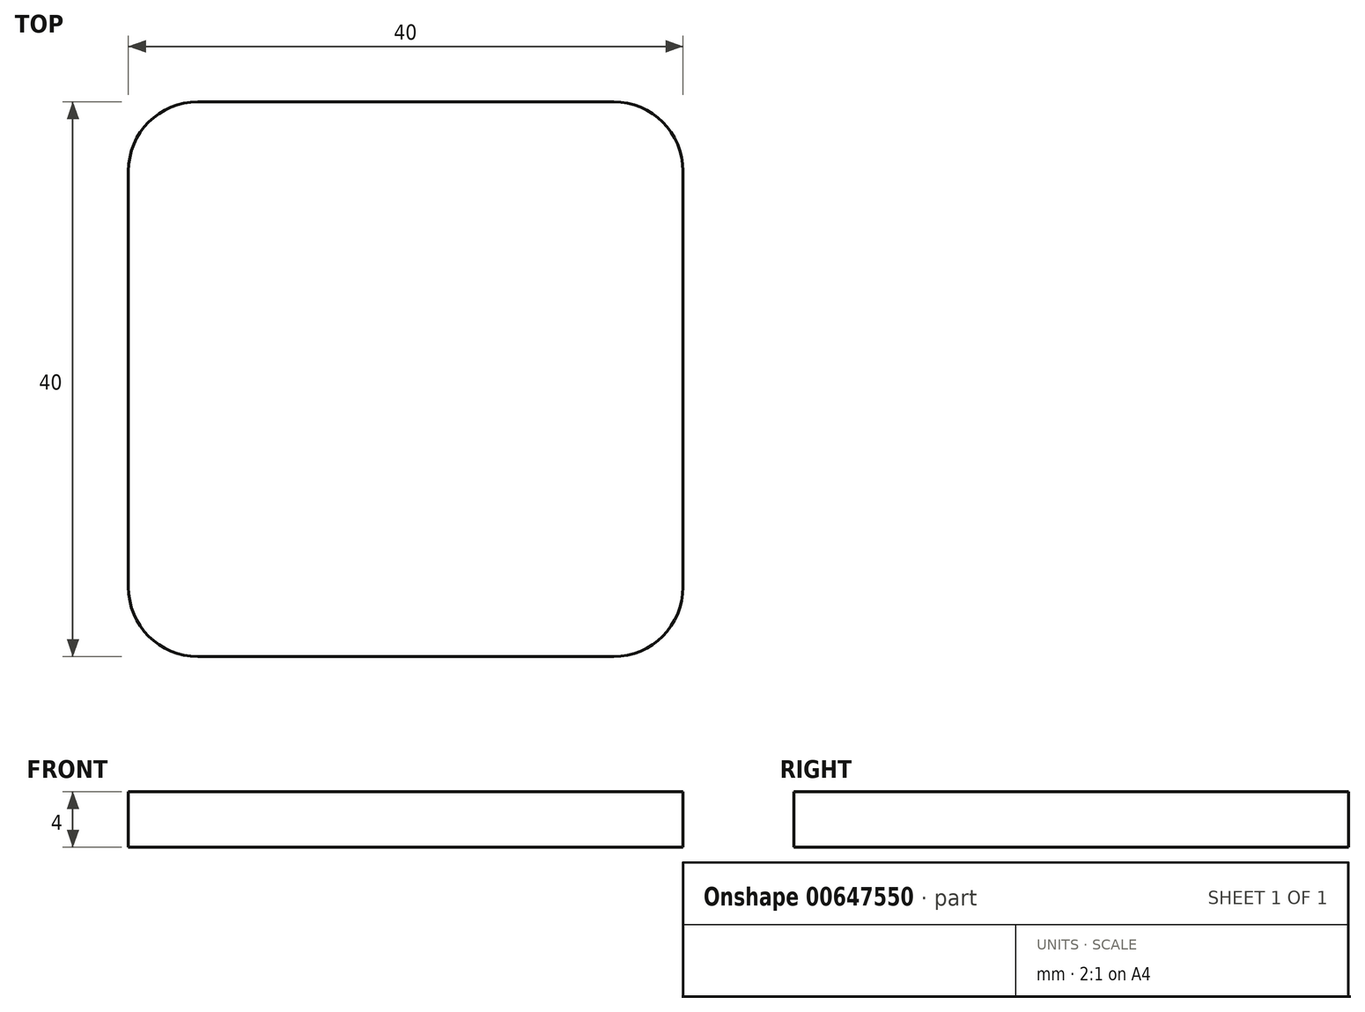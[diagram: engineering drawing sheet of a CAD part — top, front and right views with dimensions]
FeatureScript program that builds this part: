
annotation { "Feature Type Name" : "Feature", "Feature Type Description" : "" }
export const myFeature = defineFeature(function(context is Context, id is Id, definition is map)
    precondition{}
    {
        {
            var Q0;
            Q0=qCreatedBy(makeId("Top.planeOp"),FACE);
            var sketch = newSketch(context, id + "F0", { "sketchPlane" : qUnion([Q0])});
            skLineSegment(sketch, "E0.bottom", {"start": v(15, -20) * mm, "end": v(-15, -20) * mm});
            skLineSegment(sketch, "E0.top", {"start": v(15, 20) * mm, "end": v(-15, 20) * mm});
            skLineSegment(sketch, "E0.left", {"start": v(20, -15) * mm, "end": v(20, 15) * mm});
            skLineSegment(sketch, "E0.right", {"start": v(-20, -15) * mm, "end": v(-20, 15) * mm});
            skPoint(sketch, "E0.middle", {"position": v(0, 0) * mm});
            skPoint(sketch, "E1.visualSharp", {"position": v(-20, -20) * mm});
            skArc(sketch, "E1.filletArc", {"start": v(-20, -15) * mm, "mid": v(-18.54, -18.54) * mm, "end": v(-15, -20) * mm});
            skPoint(sketch, "E2.visualSharp", {"position": v(-20, 20) * mm});
            skArc(sketch, "E2.filletArc", {"start": v(-15, 20) * mm, "mid": v(-18.54, 18.54) * mm, "end": v(-20, 15) * mm});
            skPoint(sketch, "E3.visualSharp", {"position": v(20, 20) * mm});
            skArc(sketch, "E3.filletArc", {"start": v(20, 15) * mm, "mid": v(18.54, 18.54) * mm, "end": v(15, 20) * mm});
            skPoint(sketch, "E4.visualSharp", {"position": v(20, -20) * mm});
            skArc(sketch, "E4.filletArc", {"start": v(15, -20) * mm, "mid": v(18.54, -18.54) * mm, "end": v(20, -15) * mm});
            skSolve(sketch);
        }
        {
            var Q0;
            Q0=makeQuery(id+"F0.imprint","IMPRINT",FACE,{"disambiguationData":[TD([[makeQuery(id+"F0.imprint","IMPRINT",EDGE,{"derivedFrom":sQuery(id+"F0.wireOp",EDGE,"E0.bottom")}),-1.0]])]});
            extrude(context, id + "F1", {"entities" : qUnion([Q0]), "depth" : 4 * mm, "offsetDistance" : 25 * mm});
        }
    });
